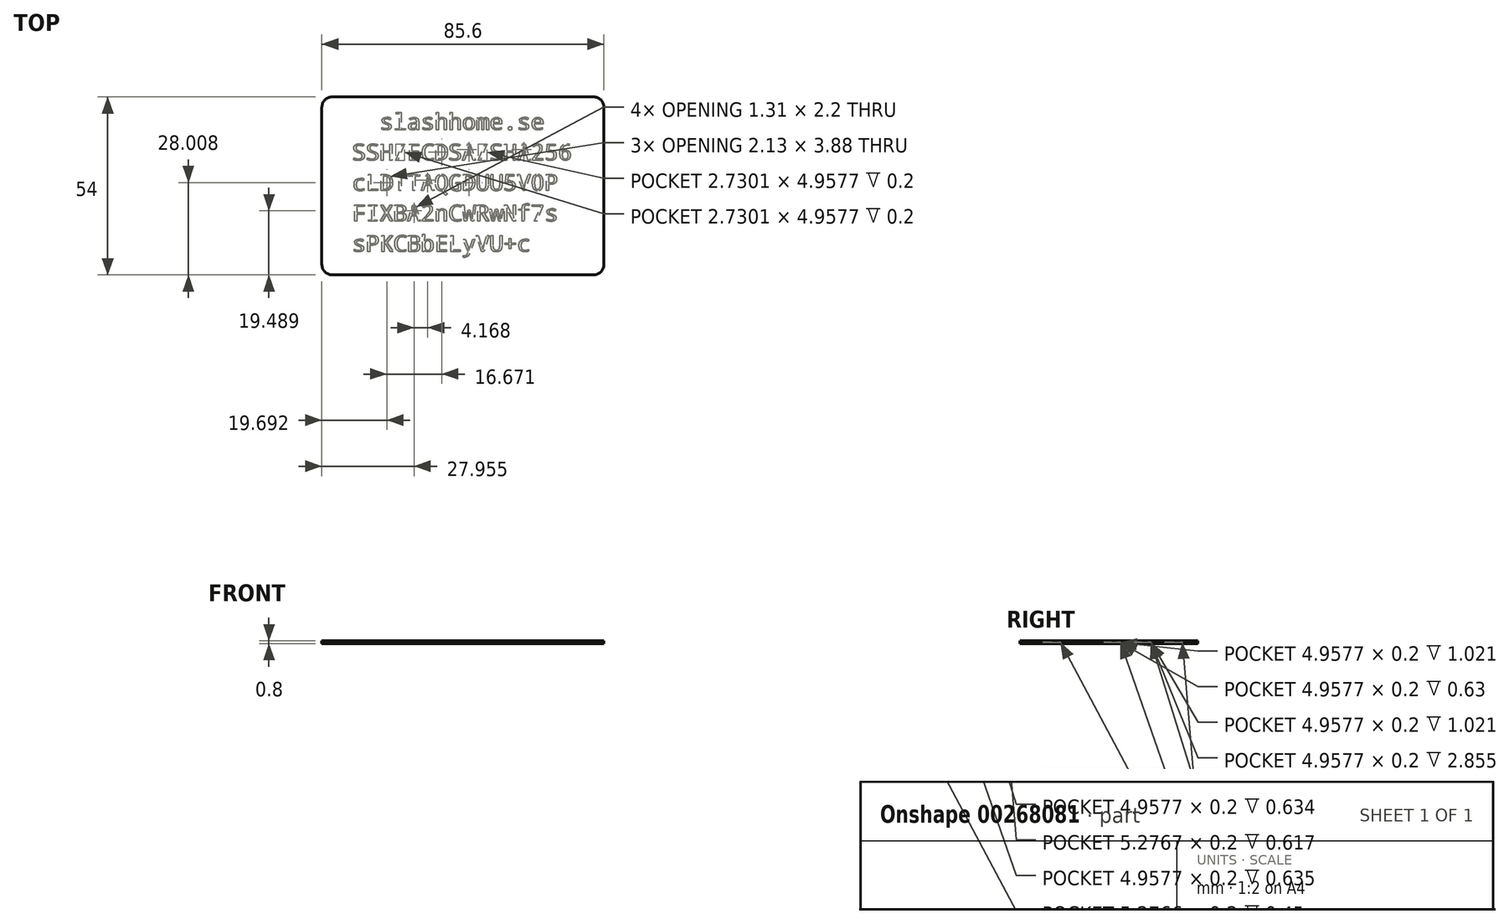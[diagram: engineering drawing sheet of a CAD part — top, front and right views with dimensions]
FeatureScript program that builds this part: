
annotation { "Feature Type Name" : "Feature", "Feature Type Description" : "" }
export const myFeature = defineFeature(function(context is Context, id is Id, definition is map)
    precondition{}
    {
        {
            var Q0;
            Q0=qCreatedBy(makeId("Top.planeOp"),FACE);
            var sketch = newSketch(context, id + "F0", { "sketchPlane" : qUnion([Q0])});
            skLineSegment(sketch, "E0.bottom", {"start": v(39.62, 27) * mm, "end": v(-39.62, 27) * mm});
            skLineSegment(sketch, "E0.top", {"start": v(39.62, -27) * mm, "end": v(-39.62, -27) * mm});
            skLineSegment(sketch, "E0.left", {"start": v(42.8, 23.82) * mm, "end": v(42.8, -23.82) * mm});
            skLineSegment(sketch, "E0.right", {"start": v(-42.8, 23.82) * mm, "end": v(-42.8, -23.82) * mm});
            skPoint(sketch, "E0.middle", {"position": v(0, 0) * mm});
            skPoint(sketch, "E1.visualSharp", {"position": v(-42.8, 27) * mm});
            skArc(sketch, "E1.filletArc", {"start": v(-39.62, 27) * mm, "mid": v(-41.87, 26.07) * mm, "end": v(-42.8, 23.82) * mm});
            skPoint(sketch, "E2.visualSharp", {"position": v(-42.8, -27) * mm});
            skArc(sketch, "E2.filletArc", {"start": v(-42.8, -23.82) * mm, "mid": v(-41.87, -26.07) * mm, "end": v(-39.62, -27) * mm});
            skPoint(sketch, "E3.visualSharp", {"position": v(42.8, -27) * mm});
            skArc(sketch, "E3.filletArc", {"start": v(39.62, -27) * mm, "mid": v(41.87, -26.07) * mm, "end": v(42.8, -23.82) * mm});
            skPoint(sketch, "E4.visualSharp", {"position": v(42.8, 27) * mm});
            skArc(sketch, "E4.filletArc", {"start": v(42.8, 23.82) * mm, "mid": v(41.87, 26.07) * mm, "end": v(39.62, 27) * mm});
            skSolve(sketch);
        }
        {
            var Q0;
            Q0=makeQuery(id+"F0.imprint","IMPRINT",FACE,{"disambiguationData":[TD([[makeQuery(id+"F0.imprint","IMPRINT",EDGE,{"derivedFrom":sQuery(id+"F0.wireOp",EDGE,"E0.bottom")}),1.0]])]});
            extrude(context, id + "F1", {"entities" : qUnion([Q0]), "endBound" : BoundingType.SYMMETRIC, "depth" : 0.8 * mm});
        }
        {
            var Q0;
            Q0=qCreatedBy(makeId("Top.planeOp"),FACE);
            var sketch = newSketch(context, id + "F2", { "sketchPlane" : qUnion([Q0])});
            skText(sketch, "E5", { "text": "  slashhome.se\nSSH/ECDSA/SHA256\ncLDTTAQGDUU5V0P\nFIXBA2nCWRwNf7s\nsPKCBbELyVU+c", "fontName": "DroidSansMono.ttf"});
            const initialGuessF2  = {"E5": [-0.0336, 0.017, 1, 0, 0.005]};
            skSetInitialGuess(sketch, initialGuessF2);
            skSolve(sketch);
        }
        {
            var Q0;
            Q0 = qSketchRegion(id + "F2", true);
            extrude(context, id + "F3", {"entities" : qUnion([Q0]), "operationType" : NewBodyOperationType.REMOVE, "endBound" : BoundingType.SYMMETRIC, "depth" : 0.2 * mm});
        }
    });
